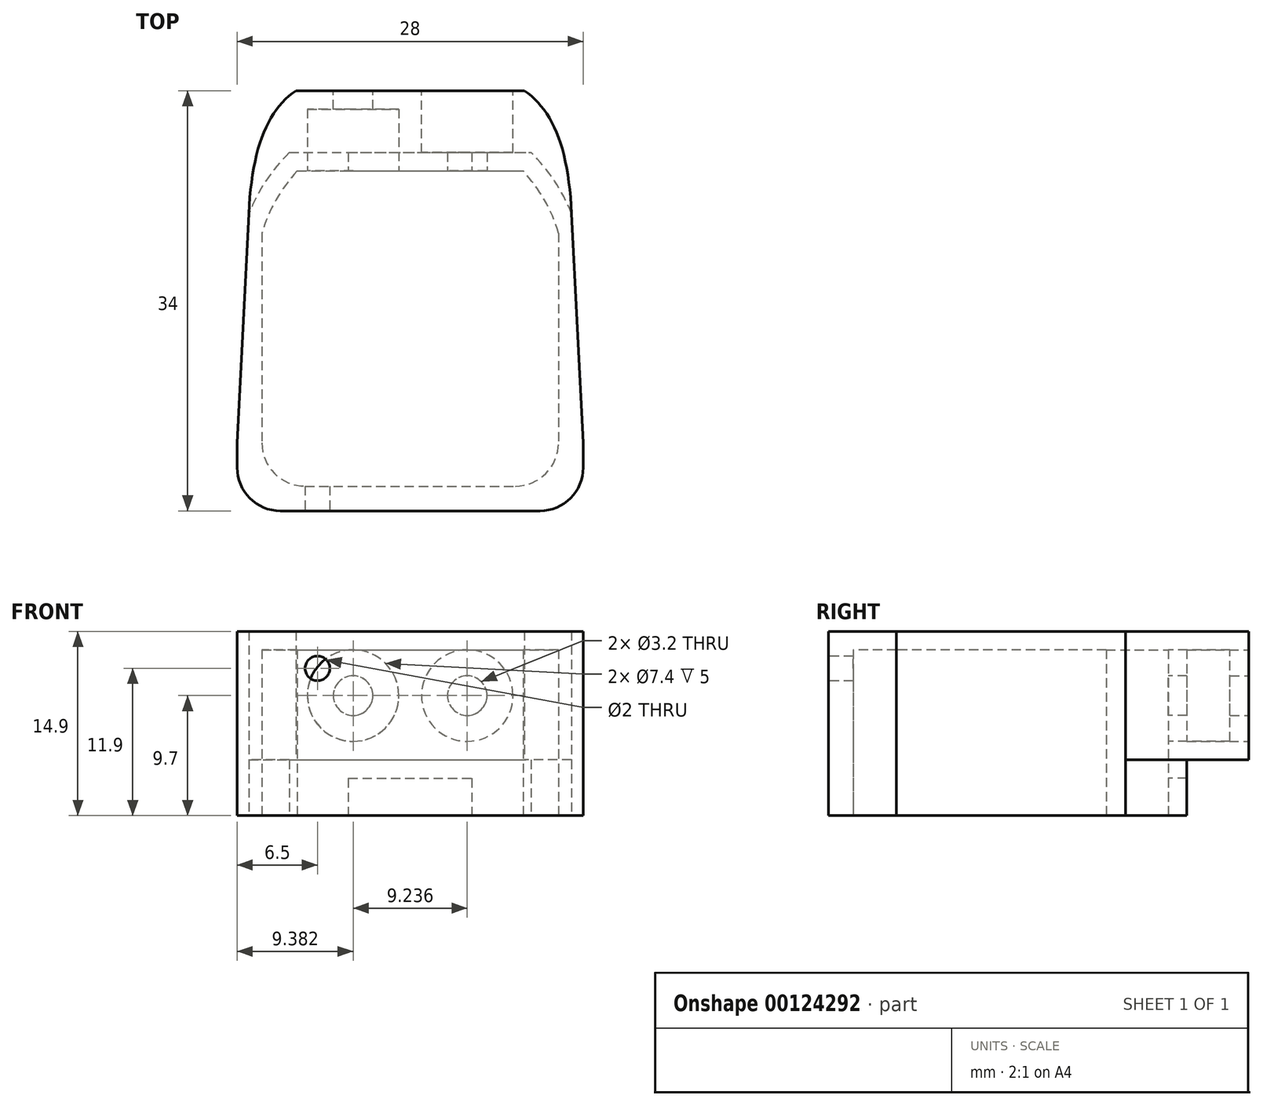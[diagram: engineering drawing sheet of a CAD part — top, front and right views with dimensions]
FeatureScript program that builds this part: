
annotation { "Feature Type Name" : "Feature", "Feature Type Description" : "" }
export const myFeature = defineFeature(function(context is Context, id is Id, definition is map)
    precondition{}
    {
        {
            var Q0;
            Q0=qCreatedBy(makeId("Top.planeOp"),FACE);
            var sketch = newSketch(context, id + "F0", { "sketchPlane" : qUnion([Q0])});
            skLineSegment(sketch, "E0", {"start": v(0, 25.65) * mm, "end": v(0, -25.65) * mm, "construction": true});
            skLineSegment(sketch, "E1", {"start": v(-14, 7.7) * mm, "end": v(-14, -11.8) * mm, "construction": true});
            skLineSegment(sketch, "E2", {"start": v(-10.5, -17.3) * mm, "end": v(-6.75, -17.3) * mm});
            skLineSegment(sketch, "E3", {"start": v(-6.75, -17.3) * mm, "end": v(-6.75, -22.3) * mm, "construction": true});
            skLineSegment(sketch, "E4", {"start": v(-6.75, -22.3) * mm, "end": v(0, -22.3) * mm, "construction": true});
            skLineSegment(sketch, "E5.0", {"start": v(-12, 5.18) * mm, "end": v(-12, -11.8) * mm, "construction": true});
            skLineSegment(sketch, "E6.0", {"start": v(-8.5, -15.3) * mm, "end": v(0, -15.3) * mm, "construction": true});
            skPoint(sketch, "E7.visualSharp", {"position": v(-14, -17.3) * mm});
            skArc(sketch, "E7.filletArc", {"start": v(-14, -13.8) * mm, "mid": v(-12.97, -16.28) * mm, "end": v(-10.5, -17.3) * mm});
            skPoint(sketch, "E8.visualSharp", {"position": v(-12, -15.3) * mm});
            skArc(sketch, "E8.filletArc", {"start": v(-12, -11.8) * mm, "mid": v(-10.97, -14.28) * mm, "end": v(-8.5, -15.3) * mm, "construction": true});
            skLineSegment(sketch, "E9", {"start": v(-14, -11.8) * mm, "end": v(-13.05, 6.75) * mm});
            skPoint(sketch, "E10.orphan", {"position": v(-12, 27.2) * mm});
            skLineSegment(sketch, "E11", {"start": v(-14, -11.8) * mm, "end": v(-14, -13.8) * mm});
            skPoint(sketch, "E12.MirrorP", {"position": v(12, 27.2) * mm});
            skPoint(sketch, "E13.visualSharp", {"position": v(-13, 7.7) * mm});
            skLineSegment(sketch, "E14.MirrorCS", {"start": v(6.75, -22.3) * mm, "end": v(0, -22.3) * mm, "construction": true});
            skLineSegment(sketch, "E15.MirrorCS", {"start": v(8.5, -15.3) * mm, "end": v(0, -15.3) * mm, "construction": true});
            skLineSegment(sketch, "E16.MirrorCS", {"start": v(14, -11.8) * mm, "end": v(14, -13.8) * mm});
            skLineSegment(sketch, "E17.MirrorCS", {"start": v(14, -11.8) * mm, "end": v(13.05, 6.75) * mm});
            skLineSegment(sketch, "E18.MirrorCS", {"start": v(10.5, -17.3) * mm, "end": v(6.75, -17.3) * mm});
            skLineSegment(sketch, "E19.MirrorCS", {"start": v(12, 5.18) * mm, "end": v(12, -11.8) * mm, "construction": true});
            skLineSegment(sketch, "E20.MirrorCS", {"start": v(6.75, -17.3) * mm, "end": v(6.75, -22.3) * mm, "construction": true});
            skPoint(sketch, "E21.MirrorP", {"position": v(13, 7.7) * mm});
            skArc(sketch, "E22.MirrorCS", {"start": v(14, -13.8) * mm, "mid": v(12.97, -16.28) * mm, "end": v(10.5, -17.3) * mm});
            skArc(sketch, "E23.MirrorCS", {"start": v(12, -11.8) * mm, "mid": v(10.97, -14.28) * mm, "end": v(8.5, -15.3) * mm, "construction": true});
            skPoint(sketch, "E24.MirrorP", {"position": v(12, -15.3) * mm});
            skPoint(sketch, "E25.MirrorP", {"position": v(14, -17.3) * mm});
            skLineSegment(sketch, "E26", {"start": v(-6.75, -17.3) * mm, "end": v(6.75, -17.3) * mm});
            skArc(sketch, "E27", {"start": v(13.05, 6.75) * mm, "mid": v(11.68, 9.4) * mm, "end": v(9.78, 11.7) * mm});
            skLineSegment(sketch, "E28", {"start": v(-9.78, 11.7) * mm, "end": v(9.78, 11.7) * mm});
            skArc(sketch, "E29.trimOffspring", {"start": v(-9.78, 11.7) * mm, "mid": v(-11.68, 9.4) * mm, "end": v(-13.05, 6.75) * mm});
            skArc(sketch, "E30.0", {"start": v(-9.15, 10.2) * mm, "mid": v(-10.87, 7.86) * mm, "end": v(-12, 5.18) * mm, "construction": true});
            skLineSegment(sketch, "E30.1", {"start": v(-9.15, 10.2) * mm, "end": v(9.15, 10.2) * mm, "construction": true});
            skArc(sketch, "E30.2", {"start": v(12, 5.18) * mm, "mid": v(10.87, 7.86) * mm, "end": v(9.15, 10.2) * mm, "construction": true});
            skPoint(sketch, "E31.orphan", {"position": v(12, 5.7) * mm});
            skPoint(sketch, "E32.orphan", {"position": v(-12, 5.7) * mm});
            skSolve(sketch);
        }
        {
            var Q0;
            Q0 = qSketchRegion(id + "F0", true);
            extrude(context, id + "F1", {"entities" : qUnion([Q0]), "depth" : 4.5 * mm});
        }
        {
            var Q0;
            Q0=makeQuery(id+"F1.opExtrude","CAP_FACE",FACE,{"disambiguationData":[OSD([sQuery(id+"F0.wireOp",EDGE,"E2"),sQuery(id+"F0.wireOp",EDGE,"E3"),sQuery(id+"F0.wireOp",EDGE,"E4"),sQuery(id+"F0.wireOp",EDGE,"E5.0"),sQuery(id+"F0.wireOp",EDGE,"E6.0"),sQuery(id+"F0.wireOp",EDGE,"E7.filletArc"),sQuery(id+"F0.wireOp",EDGE,"E8.filletArc"),sQuery(id+"F0.wireOp",EDGE,"E9"),sQuery(id+"F0.wireOp",EDGE,"nDUU9yu4-BAJh-0Tk2-GULV-rpJdPAUczq4k"),sQuery(id+"F0.wireOp",EDGE,"E11"),sQuery(id+"F0.wireOp",EDGE,"a1248285-0679-46b4-846e-51d2bdb7f2fb.0"),sQuery(id+"F0.wireOp",EDGE,"E13.filletArc"),sQuery(id+"F0.wireOp",EDGE,"fb1308a6-4672-4028-900c-11f621d318f00.MirrorCS"),sQuery(id+"F0.wireOp",EDGE,"E14.MirrorCS"),sQuery(id+"F0.wireOp",EDGE,"E15.MirrorCS"),sQuery(id+"F0.wireOp",EDGE,"E16.MirrorCS"),sQuery(id+"F0.wireOp",EDGE,"E17.MirrorCS"),sQuery(id+"F0.wireOp",EDGE,"E18.MirrorCS"),sQuery(id+"F0.wireOp",EDGE,"fb1308a6-4672-4028-900c-11f621d318f06.MirrorCS"),sQuery(id+"F0.wireOp",EDGE,"fb1308a6-4672-4028-900c-11f621d318f07.MirrorCS"),sQuery(id+"F0.wireOp",EDGE,"E19.MirrorCS"),sQuery(id+"F0.wireOp",EDGE,"E20.MirrorCS"),sQuery(id+"F0.wireOp",EDGE,"E22.MirrorCS"),sQuery(id+"F0.wireOp",EDGE,"E23.MirrorCS")])],"isStart":false});
            var sketch = newSketch(context, id + "F2", { "sketchPlane" : qUnion([Q0])});
            skLineSegment(sketch, "E33.0", {"start": v(14, -11.8) * mm, "end": v(13.05, 6.75) * mm});
            skLineSegment(sketch, "E33.1", {"start": v(-14, -11.8) * mm, "end": v(-14, -11.8) * mm});
            skLineSegment(sketch, "E33.2", {"start": v(-14, -11.8) * mm, "end": v(-14, -13.8) * mm});
            skArc(sketch, "E33.3", {"start": v(-14, -13.8) * mm, "mid": v(-12.97, -16.28) * mm, "end": v(-10.5, -17.3) * mm});
            skLineSegment(sketch, "E33.4", {"start": v(-10.5, -17.3) * mm, "end": v(10.5, -17.3) * mm});
            skLineSegment(sketch, "E33.5", {"start": v(10.5, -17.3) * mm, "end": v(10.5, -17.3) * mm});
            skArc(sketch, "E33.6", {"start": v(14, -13.8) * mm, "mid": v(12.97, -16.28) * mm, "end": v(10.5, -17.3) * mm});
            skLineSegment(sketch, "E33.7", {"start": v(14, -11.8) * mm, "end": v(14, -13.8) * mm});
            skPoint(sketch, "E34.orphan", {"position": v(-10.5, -17.3) * mm});
            skLineSegment(sketch, "E35", {"start": v(-9.24, 16.7) * mm, "end": v(9.24, 16.7) * mm});
            skPoint(sketch, "E36.orphan", {"position": v(13.05, 6.75) * mm});
            skLineSegment(sketch, "E37.0", {"start": v(-14, -11.8) * mm, "end": v(-13.05, 6.75) * mm});
            skFitSpline(sketch, "E38", {"points": [v(-13.05, 6.75) * mm, v(-9.24, 16.7) * mm], "startDerivative": vector(0.61, 15.79) * mm, "endDerivative": vector(6.85, 4.6) * mm});
            skFitSpline(sketch, "E39.MirrorCS", {"points": [v(13.05, 6.75) * mm, v(9.24, 16.7) * mm], "startDerivative": vector(-0.61, 15.79) * mm, "endDerivative": vector(-6.85, 4.6) * mm});
            skSolve(sketch);
        }
        {
            var Q0;
            Q0 = qSketchRegion(id + "F2", true);
            extrude(context, id + "F3", {"entities" : qUnion([Q0]), "operationType" : NewBodyOperationType.ADD, "depth" : 10.4 * mm});
        }
        {
            var Q0;
            Q0=makeQuery(id+"F0.imprint","IMPRINT",FACE,{"disambiguationData":[TD([[makeQuery(id+"F0.imprint","IMPRINT",EDGE,{"derivedFrom":sQuery(id+"F0.wireOp",EDGE,"E2")}),1.0]])]});
            var sketch = newSketch(context, id + "F4", { "sketchPlane" : qUnion([Q0])});
            skLineSegment(sketch, "E40.0", {"start": v(8.5, -15.3) * mm, "end": v(0, -15.3) * mm});
            skLineSegment(sketch, "E40.1", {"start": v(-8.5, -15.3) * mm, "end": v(0, -15.3) * mm});
            skArc(sketch, "E40.2", {"start": v(12, -11.8) * mm, "mid": v(10.97, -14.28) * mm, "end": v(8.5, -15.3) * mm});
            skLineSegment(sketch, "E40.3", {"start": v(12, 5.18) * mm, "end": v(12, -11.8) * mm});
            skLineSegment(sketch, "E40.4", {"start": v(-12, 5.18) * mm, "end": v(-12, -11.8) * mm});
            skArc(sketch, "E40.5", {"start": v(-12, -11.8) * mm, "mid": v(-10.97, -14.28) * mm, "end": v(-8.5, -15.3) * mm});
            skArc(sketch, "E41.0", {"start": v(-9.15, 10.2) * mm, "mid": v(-10.87, 7.86) * mm, "end": v(-12, 5.18) * mm});
            skLineSegment(sketch, "E41.1", {"start": v(-9.15, 10.2) * mm, "end": v(9.15, 10.2) * mm});
            skArc(sketch, "E41.2", {"start": v(12, 5.18) * mm, "mid": v(10.87, 7.86) * mm, "end": v(9.15, 10.2) * mm});
            skSolve(sketch);
        }
        {
            var Q0;
            Q0 = qSketchRegion(id + "F4", true);
            extrude(context, id + "F5", {"entities" : qUnion([Q0]), "operationType" : NewBodyOperationType.REMOVE, "depth" : 13.4 * mm});
        }
        {
            var Q0;
            Q0=makeQuery(id+"F3.opExtrude","SWEPT_FACE",FACE,{"disambiguationData":[OSD([sQuery(id+"F2.wireOp",EDGE,"E35")])]});
            var sketch = newSketch(context, id + "F6", { "sketchPlane" : qUnion([Q0])});
            skLineSegment(sketch, "E42", {"start": v(0, 0) * mm, "end": v(0, 14.9) * mm, "construction": true});
            skLineSegment(sketch, "E43", {"start": v(-9.24, 9.7) * mm, "end": v(0, 9.7) * mm, "construction": true});
            skCircle(sketch, "E44", {"center": v(-4.62, 9.7) * mm, "radius": 3.7 * mm});
            skCircle(sketch, "E45", {"center": v(4.62, 9.7) * mm, "radius": 1.6 * mm});
            skLineSegment(sketch, "E46", {"start": v(0, 9.7) * mm, "end": v(9.24, 9.7) * mm, "construction": true});
            skSolve(sketch);
        }
        {
            var Q0;
            Q0 = qSketchRegion(id + "F6", true);
            extrude(context, id + "F7", {"entities" : qUnion([Q0]), "operationType" : NewBodyOperationType.REMOVE, "oppositeDirection" : true, "depth" : 5 * mm});
        }
        {
            var Q0;
            Q0=makeQuery(id+"F5.boolean.opBoolean","COPY",FACE,{"derivedFrom":makeQuery(id+"F5.opExtrude","SWEPT_FACE",FACE,{"disambiguationData":[OSD([sQuery(id+"F4.wireOp",EDGE,"E41.1")])]})});
            var sketch = newSketch(context, id + "F8", { "sketchPlane" : qUnion([Q0])});
            skPoint(sketch, "E47.0", {"position": v(4.62, 9.7) * mm});
            skPoint(sketch, "E47.1", {"position": v(-4.62, 9.7) * mm});
            skCircle(sketch, "E48", {"center": v(4.62, 9.7) * mm, "radius": 1.6 * mm});
            skCircle(sketch, "E49", {"center": v(-4.62, 9.7) * mm, "radius": 3.7 * mm});
            skSolve(sketch);
        }
        {
            var Q0;
            Q0 = qSketchRegion(id + "F8", true);
            extrude(context, id + "F9", {"entities" : qUnion([Q0]), "operationType" : NewBodyOperationType.REMOVE, "oppositeDirection" : true, "depth" : 5 * mm});
        }
        {
            var Q0;
            Q0=makeQuery(id+"F3.boolean.opBoolean","MERGE",FACE,{"derivedFrom":[makeQuery(id+"F1.opExtrude","SWEPT_FACE",FACE,{"disambiguationData":[OSD([sQuery(id+"F0.wireOp",EDGE,"E2")])]}),makeQuery(id+"F1.opExtrude","SWEPT_FACE",FACE,{"disambiguationData":[OSD([sQuery(id+"F0.wireOp",EDGE,"E18.MirrorCS")])]}),makeQuery(id+"F3.opExtrude","SWEPT_FACE",FACE,{"disambiguationData":[OSD([sQuery(id+"F2.wireOp",EDGE,"E33.4"),sQuery(id+"F2.wireOp",EDGE,"E33.5")])]})]});
            var sketch = newSketch(context, id + "F10", { "sketchPlane" : qUnion([Q0])});
            skCircle(sketch, "E50", {"center": v(-7.5, 11.9) * mm, "radius": 1 * mm});
            skSolve(sketch);
        }
        {
            var Q0;
            Q0 = qSketchRegion(id + "F10", true);
            var Q1;
            Q1=makeQuery(id+"F5.boolean.opBoolean","COPY",FACE,{"derivedFrom":makeQuery(id+"F5.opExtrude","SWEPT_FACE",FACE,{"disambiguationData":[OSD([sQuery(id+"F4.wireOp",EDGE,"E40.0"),sQuery(id+"F4.wireOp",EDGE,"E40.1")])]})});
            extrude(context, id + "F11", {"entities" : qUnion([Q0]), "operationType" : NewBodyOperationType.REMOVE, "endBound" : BoundingType.UP_TO_SURFACE, "oppositeDirection" : true, "endBoundEntityFace" : qUnion([Q1]), "depth" : 25 * mm});
        }
        {
            var Q0;
            Q0=makeQuery(id+"F1.opExtrude","CAP_FACE",FACE,{"disambiguationData":[OSD([sQuery(id+"F0.wireOp",EDGE,"E2"),sQuery(id+"F0.wireOp",EDGE,"E7.filletArc"),sQuery(id+"F0.wireOp",EDGE,"E9"),sQuery(id+"F0.wireOp",EDGE,"E11"),sQuery(id+"F0.wireOp",EDGE,"E16.MirrorCS"),sQuery(id+"F0.wireOp",EDGE,"E17.MirrorCS"),sQuery(id+"F0.wireOp",EDGE,"E18.MirrorCS"),sQuery(id+"F0.wireOp",EDGE,"E22.MirrorCS"),sQuery(id+"F0.wireOp",EDGE,"E26"),sQuery(id+"F0.wireOp",EDGE,"E27"),sQuery(id+"F0.wireOp",EDGE,"E28"),sQuery(id+"F0.wireOp",EDGE,"E29.trimOffspring")])],"isStart":true});
            var sketch = newSketch(context, id + "F12", { "sketchPlane" : qUnion([Q0])});
            skLineSegment(sketch, "E51.bottom", {"start": v(-5, -11.7) * mm, "end": v(5, -11.7) * mm});
            skLineSegment(sketch, "E51.top", {"start": v(-5, -10.2) * mm, "end": v(5, -10.2) * mm});
            skLineSegment(sketch, "E51.left", {"start": v(-5, -11.7) * mm, "end": v(-5, -10.2) * mm});
            skLineSegment(sketch, "E51.right", {"start": v(5, -11.7) * mm, "end": v(5, -10.2) * mm});
            skPoint(sketch, "E51.middle", {"position": v(0, -10.95) * mm});
            skPoint(sketch, "E51.middle.positionSnap0", {"position": v(0, -10.2) * mm});
            skPoint(sketch, "E51.centerSnap0", {"position": v(0, -10.2) * mm});
            skSolve(sketch);
        }
        {
            var Q0;
            Q0 = qSketchRegion(id + "F12", true);
            extrude(context, id + "F13", {"entities" : qUnion([Q0]), "operationType" : NewBodyOperationType.REMOVE, "oppositeDirection" : true, "depth" : 3 * mm});
        }
    });
